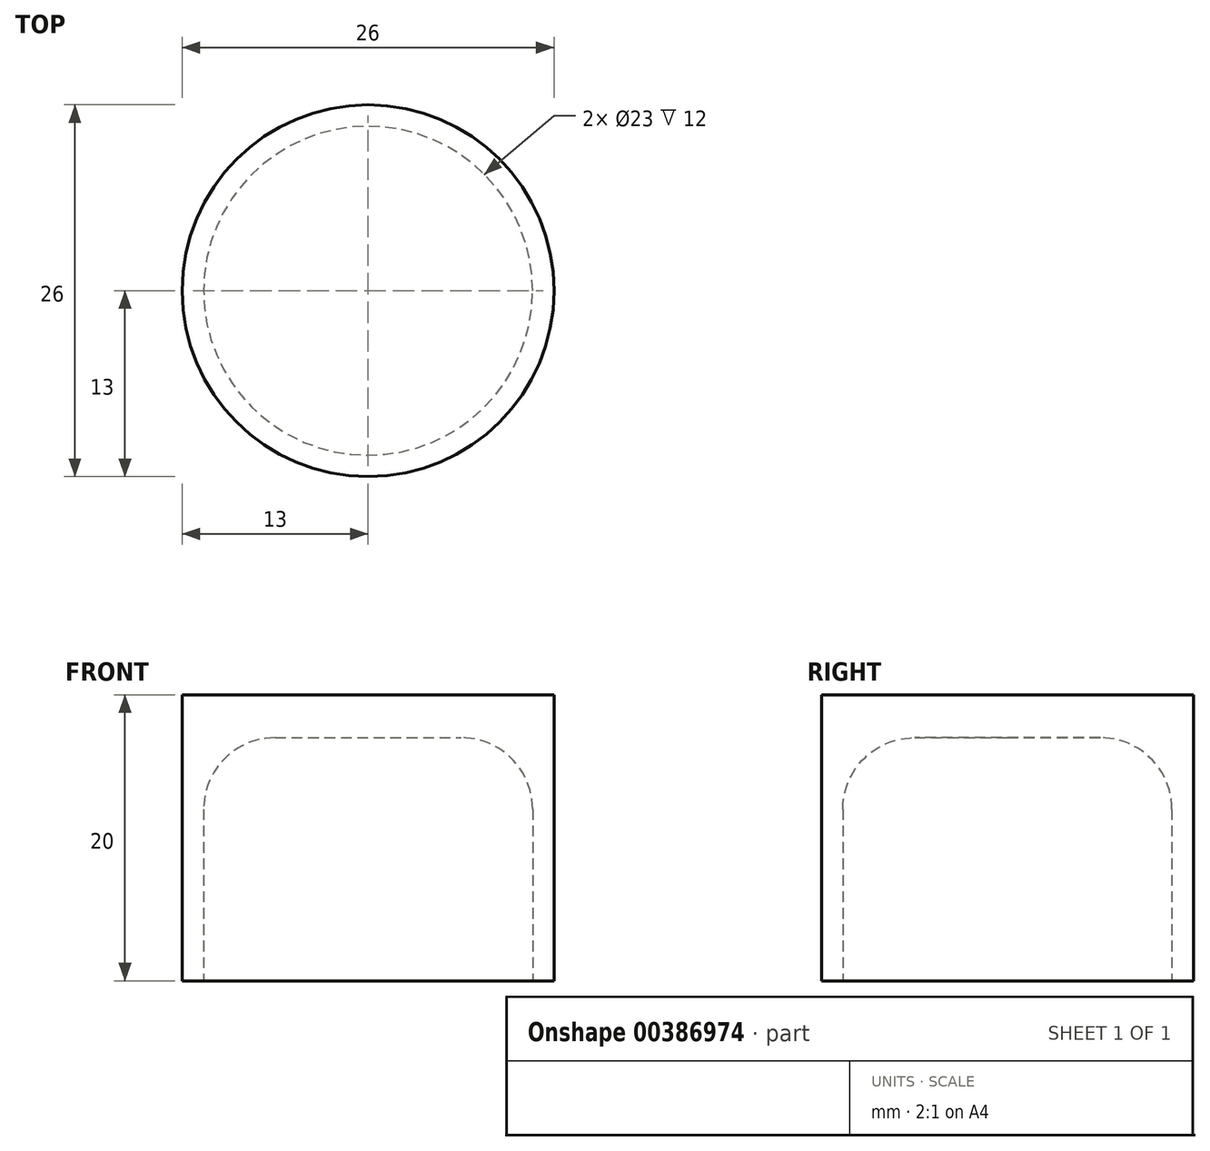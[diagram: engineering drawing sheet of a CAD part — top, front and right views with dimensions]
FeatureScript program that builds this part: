
annotation { "Feature Type Name" : "Feature", "Feature Type Description" : "" }
export const myFeature = defineFeature(function(context is Context, id is Id, definition is map)
    precondition{}
    {
        {
            var Q0;
            Q0=qCreatedBy(makeId("Top.planeOp"),FACE);
            var sketch = newSketch(context, id + "F0", { "sketchPlane" : qUnion([Q0])});
            skCircle(sketch, "E0", {"center": v(0, 0) * mm, "radius": 13 * mm});
            skSolve(sketch);
        }
        {
            var Q0;
            Q0 = qSketchRegion(id + "F0", true);
            extrude(context, id + "F1", {"entities" : qUnion([Q0]), "depth" : 20 * mm});
        }
        {
            var Q0;
            Q0=makeQuery(id+"F1.opExtrude","CAP_FACE",FACE,{"disambiguationData":[OSD([sQuery(id+"F0.wireOp",EDGE,"E0")])],"isStart":true});
            var sketch = newSketch(context, id + "F2", { "sketchPlane" : qUnion([Q0])});
            skCircle(sketch, "E1", {"center": v(0, 0) * mm, "radius": 11.5 * mm});
            skSolve(sketch);
        }
        {
            var Q0;
            Q0 = qSketchRegion(id + "F2", true);
            extrude(context, id + "F3", {"entities" : qUnion([Q0]), "operationType" : NewBodyOperationType.REMOVE, "oppositeDirection" : true, "depth" : 17 * mm});
        }
        {
            var Q0;
            Q0=makeQuery(id+"F3.boolean.opBoolean","COPY",EDGE,{"derivedFrom":makeQuery(id+"F3.opExtrude","CAP_EDGE",EDGE,{"disambiguationData":[OSD([sQuery(id+"F2.wireOp",EDGE,"E1")])],"isStart":false})});
            fillet(context, id + "F4", {"entities" : qUnion([Q0]), "radius" : 5 * mm, "tangentPropagation" : true, "allowEdgeOverflow" : false});
        }
    });
